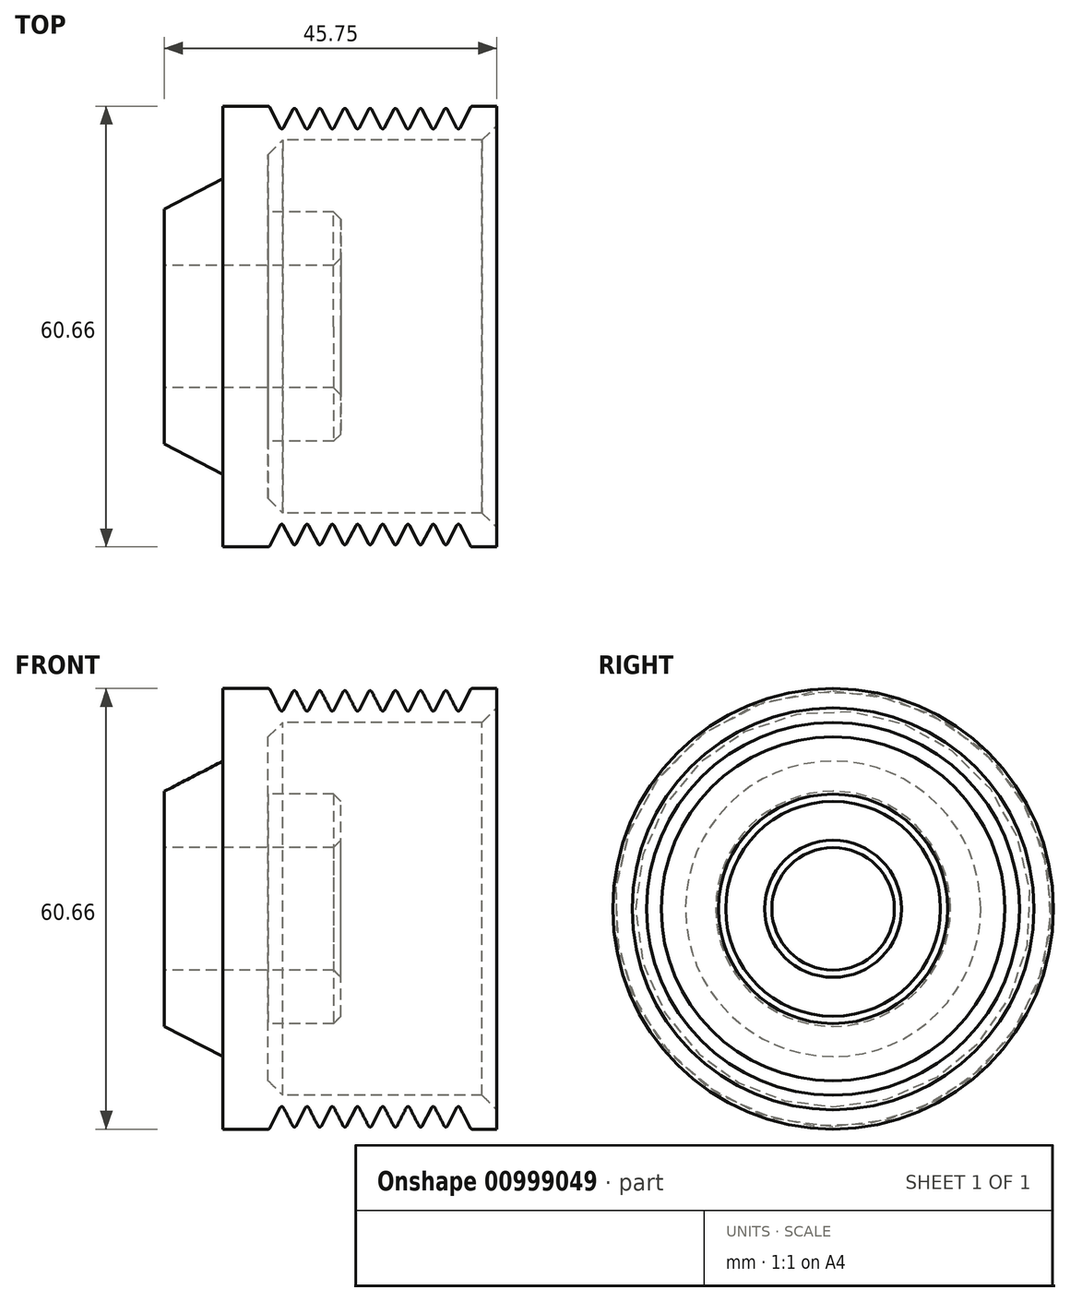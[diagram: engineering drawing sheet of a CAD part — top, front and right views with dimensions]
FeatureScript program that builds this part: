
annotation { "Feature Type Name" : "Feature", "Feature Type Description" : "" }
export const myFeature = defineFeature(function(context is Context, id is Id, definition is map)
    precondition{}
    {
        {
            var Q0;
            Q0=qCreatedBy(makeId("Front.planeOp"),FACE);
            var sketch = newSketch(context, id + "F0", { "sketchPlane" : qUnion([Q0])});
            skLineSegment(sketch, "E0", {"start": v(-38.13, 8.43) * mm, "end": v(-38.13, 16.18) * mm});
            skLineSegment(sketch, "E1", {"start": v(-38.13, 16.18) * mm, "end": v(-30.08, 20.34) * mm});
            skLineSegment(sketch, "E2", {"start": v(-30.08, 20.34) * mm, "end": v(-30.08, 30.33) * mm});
            skLineSegment(sketch, "E3", {"start": v(-13.83, 8.43) * mm, "end": v(-38.13, 8.43) * mm});
            skLineSegment(sketch, "E4", {"start": v(-45.5, 0) * mm, "end": v(-6.35, 0) * mm, "construction": true});
            skLineSegment(sketch, "E5", {"start": v(-23.83, 25.66) * mm, "end": v(-23.83, 15.79) * mm});
            skLineSegment(sketch, "E6", {"start": v(-23.83, 15.79) * mm, "end": v(-13.83, 15.8) * mm});
            skLineSegment(sketch, "E7", {"start": v(-13.83, 15.8) * mm, "end": v(-13.83, 8.43) * mm});
            skLineSegment(sketch, "E8", {"start": v(-30.08, 30.33) * mm, "end": v(-30.08, 30.33) * mm});
            skLineSegment(sketch, "E9", {"start": v(-30.08, 30.33) * mm, "end": v(7.62, 30.33) * mm});
            skLineSegment(sketch, "E10", {"start": v(7.62, 30.33) * mm, "end": v(7.62, 25.67) * mm});
            skLineSegment(sketch, "E11", {"start": v(7.62, 25.66) * mm, "end": v(-23.83, 25.66) * mm});
            skSolve(sketch);
        }
        {
            var Q0;
            Q0 = qSketchRegion(id + "F0", true);
            var Q1;
            Q1=sQuery(id+"F0.wireOp",EDGE,"E4");
            revolve(context, id + "F1", {"surfaceOperationType" : NewSurfaceOperationType.NEW, "entities" : qUnion([Q0]), "axis" : qUnion([Q1]), "revolveType" : RevolveType.FULL});
        }
        {
            var Q0;
            Q0=qCreatedBy(makeId("Front.planeOp"),FACE);
            var sketch = newSketch(context, id + "F2", { "sketchPlane" : qUnion([Q0])});
            skLineSegment(sketch, "E12", {"start": v(-30.08, 42.61) * mm, "end": v(-30.08, 2.77) * mm, "construction": true});
            skLineSegment(sketch, "E13", {"start": v(-23.7, 38.6) * mm, "end": v(-23.7, 3.3) * mm, "construction": true});
            skLineSegment(sketch, "E14", {"start": v(-23.7, 30.33) * mm, "end": v(-21.97, 26.93) * mm});
            skLineSegment(sketch, "E15", {"start": v(-21.97, 26.93) * mm, "end": v(-20.23, 30.33) * mm});
            skLineSegment(sketch, "E16", {"start": v(-20.23, 30.33) * mm, "end": v(-23.7, 30.33) * mm});
            skLineSegment(sketch, "E17", {"start": v(-20.23, 30.33) * mm, "end": v(-18.5, 26.93) * mm});
            skLineSegment(sketch, "E18", {"start": v(-18.5, 26.93) * mm, "end": v(-16.75, 30.33) * mm});
            skLineSegment(sketch, "E19", {"start": v(-16.75, 30.33) * mm, "end": v(-15.02, 26.93) * mm});
            skLineSegment(sketch, "E20", {"start": v(-15.02, 26.93) * mm, "end": v(-13.28, 30.33) * mm});
            skLineSegment(sketch, "E21", {"start": v(-6.33, 30.33) * mm, "end": v(-4.6, 26.93) * mm});
            skLineSegment(sketch, "E22", {"start": v(4.1, 30.33) * mm, "end": v(0.62, 30.33) * mm});
            skLineSegment(sketch, "E23", {"start": v(0.62, 30.33) * mm, "end": v(-2.85, 30.33) * mm});
            skLineSegment(sketch, "E24", {"start": v(-2.85, 30.33) * mm, "end": v(-6.33, 30.33) * mm});
            skLineSegment(sketch, "E25", {"start": v(-6.33, 30.33) * mm, "end": v(-9.8, 30.33) * mm});
            skLineSegment(sketch, "E26", {"start": v(-9.8, 30.33) * mm, "end": v(-13.28, 30.33) * mm});
            skLineSegment(sketch, "E27", {"start": v(-13.28, 30.33) * mm, "end": v(-16.75, 30.33) * mm});
            skLineSegment(sketch, "E28", {"start": v(-16.75, 30.33) * mm, "end": v(-20.23, 30.33) * mm});
            skLineSegment(sketch, "E29", {"start": v(-13.28, 30.33) * mm, "end": v(-11.54, 26.93) * mm});
            skLineSegment(sketch, "E30", {"start": v(-11.54, 26.93) * mm, "end": v(-9.8, 30.33) * mm});
            skLineSegment(sketch, "E31", {"start": v(-9.8, 30.33) * mm, "end": v(-8.07, 26.93) * mm});
            skLineSegment(sketch, "E32", {"start": v(-8.07, 26.93) * mm, "end": v(-6.33, 30.33) * mm});
            skLineSegment(sketch, "E33", {"start": v(-2.85, 30.33) * mm, "end": v(-4.6, 26.93) * mm});
            skLineSegment(sketch, "E34", {"start": v(-2.85, 30.33) * mm, "end": v(-1.12, 26.93) * mm});
            skLineSegment(sketch, "E35", {"start": v(-1.12, 26.93) * mm, "end": v(0.62, 30.33) * mm});
            skLineSegment(sketch, "E36", {"start": v(0.62, 30.33) * mm, "end": v(2.36, 26.93) * mm});
            skLineSegment(sketch, "E37", {"start": v(2.36, 26.93) * mm, "end": v(4.1, 30.33) * mm});
            skSolve(sketch);
        }
        {
            var Q0;
            Q0 = qSketchRegion(id + "F2", true);
            var Q1;
            Q1=sQuery(id+"F0.wireOp",EDGE,"E4");
            revolve(context, id + "F3", {"operationType" : NewBodyOperationType.REMOVE, "surfaceOperationType" : NewSurfaceOperationType.NEW, "entities" : qUnion([Q0]), "axis" : qUnion([Q1]), "revolveType" : RevolveType.FULL, "oppositeDirection" : true});
        }
        {
            var Q0;
            Q0=makeQuery(id+"F1.opRevolve","SWEPT_FACE",FACE,{"disambiguationData":[OSD([sQuery(id+"F0.wireOp",EDGE,"E11")])]});
            chamfer(context, id + "F4", {"entities" : qUnion([Q0]), "width" : 2 * mm});
        }
        {
            var Q0;
            Q0=makeQuery(id+"F1.opRevolve","SWEPT_FACE",FACE,{"disambiguationData":[OSD([sQuery(id+"F0.wireOp",EDGE,"E7")])]});
            chamfer(context, id + "F5", {"entities" : qUnion([Q0]), "width" : 1 * mm, "tangentPropagation" : true});
        }
        {
            var Q0;
            Q0=makeQuery(id+"F3.boolean.opBoolean","COPY",FACE,{"derivedFrom":makeQuery(id+"F3.opRevolve","SWEPT_FACE",FACE,{"disambiguationData":[OSD([sQuery(id+"F2.wireOp",EDGE,"E17")])]})});
            var Q1;
            Q1=makeQuery(id+"F3.boolean.opBoolean","COPY",FACE,{"derivedFrom":makeQuery(id+"F3.opRevolve","SWEPT_FACE",FACE,{"disambiguationData":[OSD([sQuery(id+"F2.wireOp",EDGE,"E14")])]})});
            var Q2;
            Q2=makeQuery(id+"F3.boolean.opBoolean","COPY",FACE,{"derivedFrom":makeQuery(id+"F3.opRevolve","SWEPT_FACE",FACE,{"disambiguationData":[OSD([sQuery(id+"F2.wireOp",EDGE,"E18")])]})});
            var Q3;
            Q3=makeQuery(id+"F3.boolean.opBoolean","COPY",FACE,{"derivedFrom":makeQuery(id+"F3.opRevolve","SWEPT_FACE",FACE,{"disambiguationData":[OSD([sQuery(id+"F2.wireOp",EDGE,"E19")])]})});
            var Q4;
            Q4=makeQuery(id+"F3.boolean.opBoolean","COPY",FACE,{"derivedFrom":makeQuery(id+"F3.opRevolve","SWEPT_FACE",FACE,{"disambiguationData":[OSD([sQuery(id+"F2.wireOp",EDGE,"E20")])]})});
            var Q5;
            Q5=makeQuery(id+"F3.boolean.opBoolean","COPY",FACE,{"derivedFrom":makeQuery(id+"F3.opRevolve","SWEPT_FACE",FACE,{"disambiguationData":[OSD([sQuery(id+"F2.wireOp",EDGE,"E29")])]})});
            var Q6;
            Q6=makeQuery(id+"F3.boolean.opBoolean","COPY",FACE,{"derivedFrom":makeQuery(id+"F3.opRevolve","SWEPT_FACE",FACE,{"disambiguationData":[OSD([sQuery(id+"F2.wireOp",EDGE,"E30")])]})});
            var Q7;
            Q7=makeQuery(id+"F3.boolean.opBoolean","COPY",FACE,{"derivedFrom":makeQuery(id+"F3.opRevolve","SWEPT_FACE",FACE,{"disambiguationData":[OSD([sQuery(id+"F2.wireOp",EDGE,"E31")])]})});
            var Q8;
            Q8=makeQuery(id+"F3.boolean.opBoolean","COPY",FACE,{"derivedFrom":makeQuery(id+"F3.opRevolve","SWEPT_FACE",FACE,{"disambiguationData":[OSD([sQuery(id+"F2.wireOp",EDGE,"E32")])]})});
            var Q9;
            Q9=makeQuery(id+"F3.boolean.opBoolean","COPY",FACE,{"derivedFrom":makeQuery(id+"F3.opRevolve","SWEPT_FACE",FACE,{"disambiguationData":[OSD([sQuery(id+"F2.wireOp",EDGE,"E21")])]})});
            var Q10;
            Q10=makeQuery(id+"F3.boolean.opBoolean","COPY",FACE,{"derivedFrom":makeQuery(id+"F3.opRevolve","SWEPT_FACE",FACE,{"disambiguationData":[OSD([sQuery(id+"F2.wireOp",EDGE,"E33")])]})});
            var Q11;
            Q11=makeQuery(id+"F3.boolean.opBoolean","COPY",FACE,{"derivedFrom":makeQuery(id+"F3.opRevolve","SWEPT_FACE",FACE,{"disambiguationData":[OSD([sQuery(id+"F2.wireOp",EDGE,"E34")])]})});
            var Q12;
            Q12=makeQuery(id+"F3.boolean.opBoolean","COPY",FACE,{"derivedFrom":makeQuery(id+"F3.opRevolve","SWEPT_FACE",FACE,{"disambiguationData":[OSD([sQuery(id+"F2.wireOp",EDGE,"E35")])]})});
            var Q13;
            Q13=makeQuery(id+"F3.boolean.opBoolean","COPY",FACE,{"derivedFrom":makeQuery(id+"F3.opRevolve","SWEPT_FACE",FACE,{"disambiguationData":[OSD([sQuery(id+"F2.wireOp",EDGE,"E36")])]})});
            var Q14;
            Q14=makeQuery(id+"F3.boolean.opBoolean","COPY",FACE,{"derivedFrom":makeQuery(id+"F3.opRevolve","SWEPT_FACE",FACE,{"disambiguationData":[OSD([sQuery(id+"F2.wireOp",EDGE,"E37")])]})});
            fillet(context, id + "F6", {"entities" : qUnion([Q0, Q1, Q2, Q3, Q4, Q5, Q6, Q7, Q8, Q9, Q10, Q11, Q12, Q13, Q14]), "radius" : .25 * mm, "tangentPropagation" : true, "allowEdgeOverflow" : false});
        }
    });
